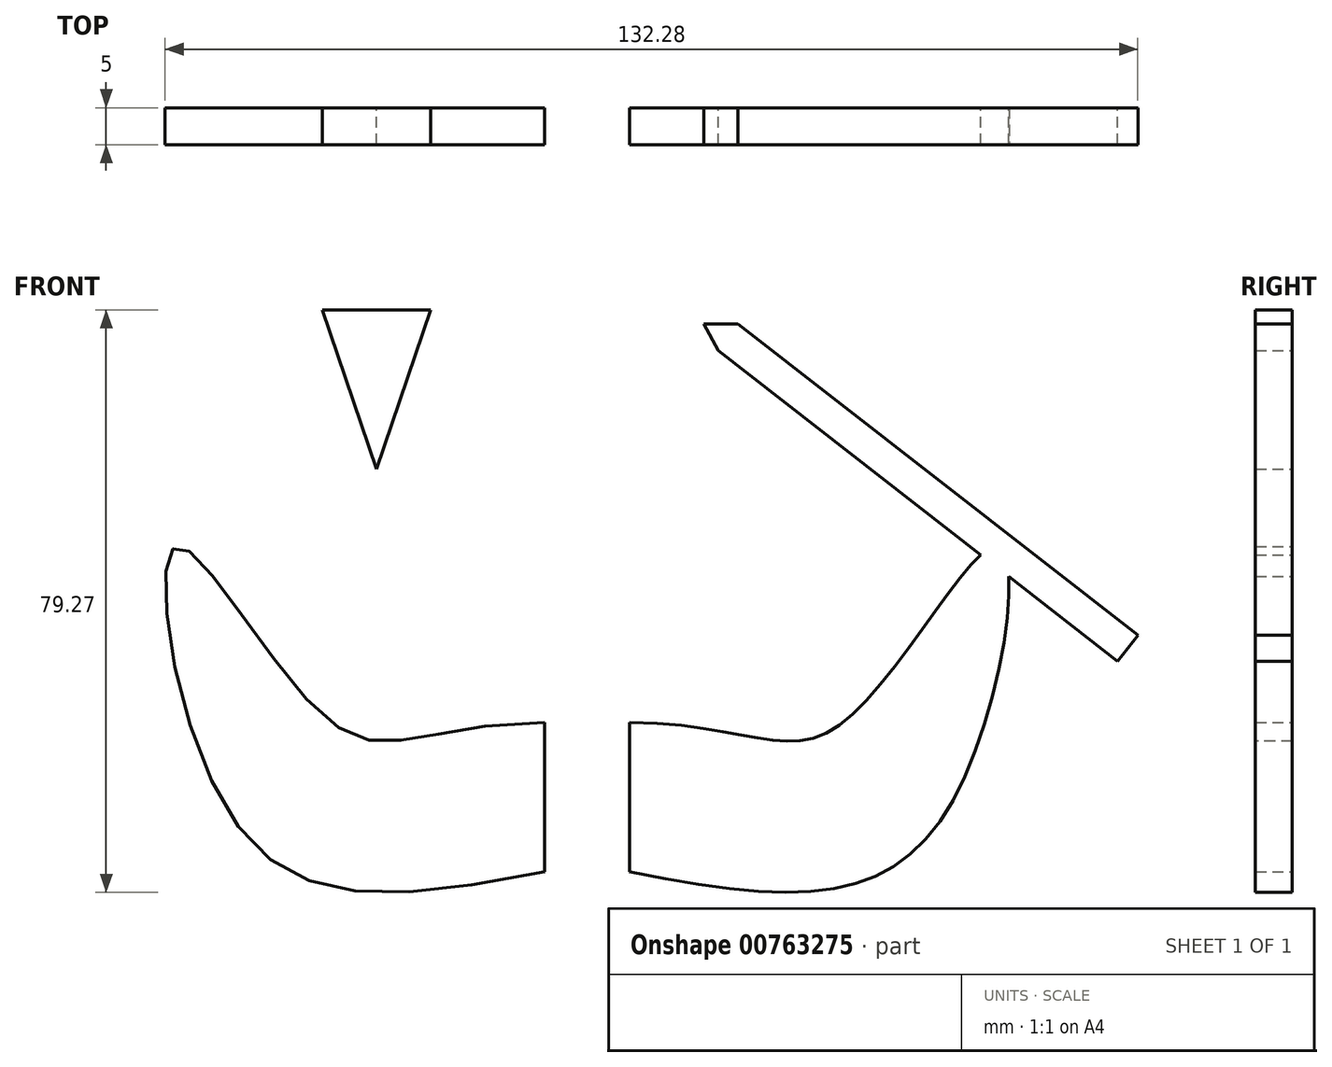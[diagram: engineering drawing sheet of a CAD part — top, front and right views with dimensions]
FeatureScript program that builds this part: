
annotation { "Feature Type Name" : "Feature", "Feature Type Description" : "" }
export const myFeature = defineFeature(function(context is Context, id is Id, definition is map)
    precondition{}
    {
        {
            var Q0;
            Q0=qCreatedBy(makeId("Front.planeOp"),FACE);
            var sketch = newSketch(context, id + "F0", { "sketchPlane" : qUnion([Q0])});
            skFitSpline(sketch, "E0", {"points": [v(0, 0) * mm, v(28.96, 0) * mm, v(50, 23.95) * mm, v(43.42, -11.5) * mm, v(0, -20.29) * mm], "startDerivative": vector(209.98, 0) * mm, "endDerivative": vector(-243.23, 50.87) * mm});
            skLineSegment(sketch, "E1", {"start": v(0, -20.29) * mm, "end": v(0, 0) * mm});
            skLineSegment(sketch, "E2", {"start": v(12.05, 50.66) * mm, "end": v(66.35, 8.36) * mm});
            skLineSegment(sketch, "E3", {"start": v(66.35, 8.36) * mm, "end": v(69.1, 11.88) * mm});
            skLineSegment(sketch, "E4", {"start": v(69.1, 11.88) * mm, "end": v(14.68, 54.28) * mm});
            skLineSegment(sketch, "E5", {"start": v(14.68, 54.28) * mm, "end": v(10.05, 54.28) * mm});
            skLineSegment(sketch, "E6", {"start": v(10.05, 54.28) * mm, "end": v(12.05, 50.66) * mm});
            skLineSegment(sketch, "E7", {"start": v(0, 0) * mm, "end": v(0, -20.29) * mm});
            skLineSegment(sketch, "E8.MirrorCS", {"start": v(-11.6, 0) * mm, "end": v(-11.6, -20.29) * mm});
            skFitSpline(sketch, "E9.MirrorCS", {"points": [v(-11.6, 0) * mm, v(-40.56, 0) * mm, v(-61.6, 23.95) * mm, v(-55.01, -11.5) * mm, v(-11.6, -20.29) * mm], "startDerivative": vector(-209.98, 0) * mm, "endDerivative": vector(243.23, 50.87) * mm});
            skLineSegment(sketch, "E10", {"start": v(-41.81, 56.16) * mm, "end": v(-27.08, 56.16) * mm});
            skLineSegment(sketch, "E11", {"start": v(-27.08, 56.16) * mm, "end": v(-34.44, 34.5) * mm});
            skLineSegment(sketch, "E12", {"start": v(-34.44, 34.5) * mm, "end": v(-41.81, 56.16) * mm});
            skSolve(sketch);
        }
        {
            var Q0;
            Q0 = qSketchRegion(id + "F0", true);
            extrude(context, id + "F1", {"entities" : qUnion([Q0]), "depth" : 5 * mm, "offsetDistance" : 25 * mm});
        }
    });
